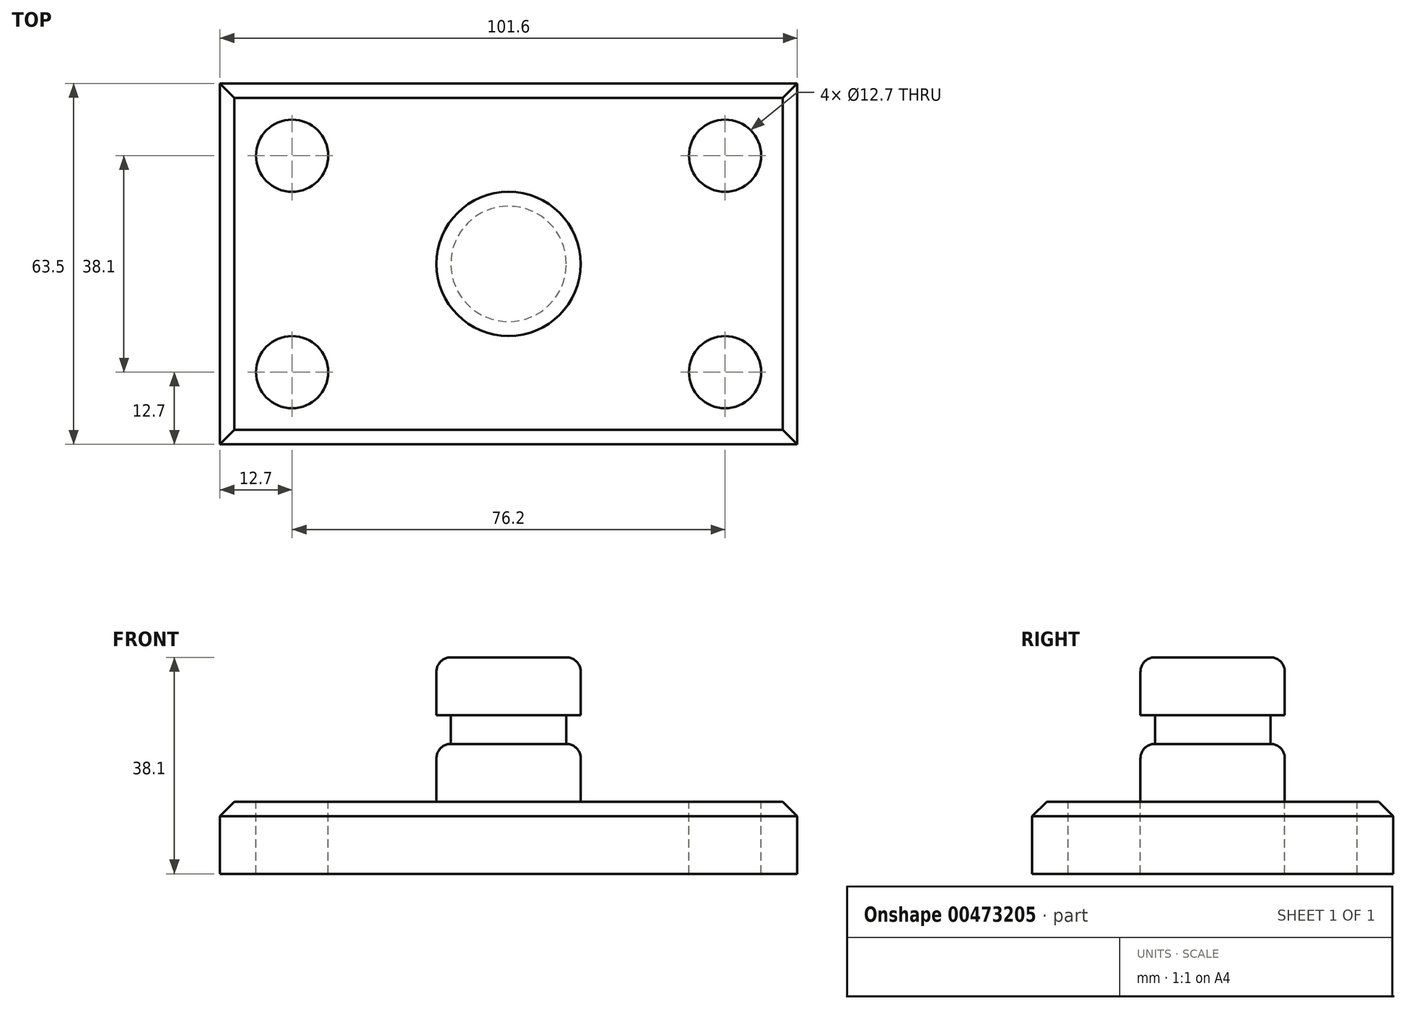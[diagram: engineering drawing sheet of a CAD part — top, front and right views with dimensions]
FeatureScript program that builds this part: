
annotation { "Feature Type Name" : "Feature", "Feature Type Description" : "" }
export const myFeature = defineFeature(function(context is Context, id is Id, definition is map)
    precondition{}
    {
        {
            var Q0;
            Q0=qCreatedBy(makeId("Top.planeOp"),FACE);
            var sketch = newSketch(context, id + "F0", { "sketchPlane" : qUnion([Q0])});
            skLineSegment(sketch, "E0.bottom", {"start": v(50.8, -31.75) * mm, "end": v(-50.8, -31.75) * mm});
            skLineSegment(sketch, "E0.top", {"start": v(50.8, 31.75) * mm, "end": v(-50.8, 31.75) * mm});
            skLineSegment(sketch, "E0.left", {"start": v(50.8, -31.75) * mm, "end": v(50.8, 31.75) * mm});
            skLineSegment(sketch, "E0.right", {"start": v(-50.8, -31.75) * mm, "end": v(-50.8, 31.75) * mm});
            skPoint(sketch, "E0.middle", {"position": v(0, 0) * mm});
            skSolve(sketch);
        }
        {
            var Q0;
            Q0=makeQuery(id+"F0.imprint","IMPRINT",FACE,{"disambiguationData":[TD([[makeQuery(id+"F0.imprint","IMPRINT",EDGE,{"derivedFrom":sQuery(id+"F0.wireOp",EDGE,"E0.bottom")}),-1.0]])]});
            extrude(context, id + "F1", {"entities" : qUnion([Q0]), "depth" : 12.7 * mm});
        }
        {
            var Q0;
            Q0=makeQuery(id+"F1.opExtrude","CAP_FACE",FACE,{"disambiguationData":[OSD([sQuery(id+"F0.wireOp",EDGE,"E0.bottom"),sQuery(id+"F0.wireOp",EDGE,"E0.top"),sQuery(id+"F0.wireOp",EDGE,"E0.left"),sQuery(id+"F0.wireOp",EDGE,"E0.right")])],"isStart":false});
            var sketch = newSketch(context, id + "F2", { "sketchPlane" : qUnion([Q0])});
            skCircle(sketch, "E1", {"center": v(-38.1, 19.05) * mm, "radius": 6.35 * mm});
            skCircle(sketch, "E2", {"center": v(38.1, 19.05) * mm, "radius": 6.35 * mm});
            skCircle(sketch, "E3", {"center": v(38.1, -19.05) * mm, "radius": 6.35 * mm});
            skCircle(sketch, "E4", {"center": v(-38.1, -19.05) * mm, "radius": 6.35 * mm});
            skSolve(sketch);
        }
        {
            var Q0;
            Q0 = qSketchRegion(id + "F2", true);
            extrude(context, id + "F3", {"entities" : qUnion([Q0]), "operationType" : NewBodyOperationType.REMOVE, "endBound" : BoundingType.THROUGH_ALL, "oppositeDirection" : true, "depth" : 25.4 * mm});
        }
        {
            var Q0;
            Q0=qCreatedBy(makeId("Front.planeOp"),FACE);
            var sketch = newSketch(context, id + "F4", { "sketchPlane" : qUnion([Q0])});
            skLineSegment(sketch, "E5.bottom", {"start": v(0, 12.7) * mm, "end": v(12.7, 12.7) * mm});
            skLineSegment(sketch, "E5.top", {"start": v(0, 38.1) * mm, "end": v(12.7, 38.1) * mm});
            skLineSegment(sketch, "E5.left", {"start": v(0, 12.7) * mm, "end": v(0, 38.1) * mm});
            skLineSegment(sketch, "E5.right", {"start": v(12.7, 12.7) * mm, "end": v(12.7, 38.1) * mm});
            skSolve(sketch);
        }
        {
            var Q0;
            Q0=makeQuery(id+"F4.imprint","IMPRINT",FACE,{"disambiguationData":[TD([[makeQuery(id+"F4.imprint","IMPRINT",EDGE,{"derivedFrom":sQuery(id+"F4.wireOp",EDGE,"E5.bottom")}),1.0]])]});
            var Q1;
            Q1=sQuery(id+"F4.wireOp",EDGE,"E5.left");
            revolve(context, id + "F5", {"operationType" : NewBodyOperationType.ADD, "entities" : qUnion([Q0]), "axis" : qUnion([Q1]), "revolveType" : RevolveType.FULL});
        }
        {
            var Q0;
            Q0=qCreatedBy(makeId("Front.planeOp"),FACE);
            var sketch = newSketch(context, id + "F6", { "sketchPlane" : qUnion([Q0])});
            skLineSegment(sketch, "E6.bottom", {"start": v(17.43, 27.94) * mm, "end": v(10.16, 27.94) * mm});
            skLineSegment(sketch, "E6.top", {"start": v(17.43, 22.86) * mm, "end": v(10.16, 22.86) * mm});
            skLineSegment(sketch, "E6.left", {"start": v(17.43, 27.94) * mm, "end": v(17.43, 22.86) * mm});
            skLineSegment(sketch, "E6.right", {"start": v(10.16, 27.94) * mm, "end": v(10.16, 22.86) * mm});
            skLineSegment(sketch, "E7", {"start": v(12.7, 38.1) * mm, "end": v(12.7, 12.7) * mm});
            skSolve(sketch);
        }
        {
            var Q0;
            Q0 = qSketchRegion(id + "F6", true);
            var Q1;
            Q1=makeQuery(id+"F5.opRevolve","SWEPT_FACE",FACE,{"disambiguationData":[OSD([sQuery(id+"F4.wireOp",EDGE,"E5.right")])]});
            revolve(context, id + "F7", {"operationType" : NewBodyOperationType.REMOVE, "entities" : qUnion([Q0]), "axis" : qUnion([Q1]), "revolveType" : RevolveType.FULL, "oppositeDirection" : true});
        }
        {
            var Q0;
            Q0=makeQuery(id+"F5.opRevolve","SWEPT_EDGE",EDGE,{"disambiguationData":[OSD([sQuery(id+"F4.wireOp",EDGE,"E5.bottom"),sQuery(id+"F4.wireOp",EDGE,"E5.right")])]});
            var Q1;
            Q1=makeQuery(id+"F7.boolean.opBoolean","INTERSECT",EDGE,{"derivedFrom":[makeQuery(id+"F5.opRevolve","SWEPT_FACE",FACE,{"disambiguationData":[OSD([sQuery(id+"F4.wireOp",EDGE,"E5.right")])]}),makeQuery(id+"F7.opRevolve","SWEPT_FACE",FACE,{"disambiguationData":[OSD([sQuery(id+"F6.wireOp",EDGE,"E6.top")])]})]});
            fillet(context, id + "F8", {"entities" : qUnion([Q0, Q1]), "radius" : 2.54 * mm, "tangentPropagation" : true, "allowEdgeOverflow" : false});
        }
        {
            var Q0;
            Q0=makeQuery(id+"F5.opRevolve","SWEPT_EDGE",EDGE,{"disambiguationData":[OSD([sQuery(id+"F4.wireOp",EDGE,"E5.top"),sQuery(id+"F4.wireOp",EDGE,"E5.right")])]});
            fillet(context, id + "F9", {"entities" : qUnion([Q0]), "radius" : 2.54 * mm, "tangentPropagation" : true, "allowEdgeOverflow" : false});
        }
        {
            var Q0;
            Q0=makeQuery(id+"F1.opExtrude","CAP_EDGE",EDGE,{"disambiguationData":[OSD([sQuery(id+"F0.wireOp",EDGE,"E0.right")])],"isStart":false});
            var Q1;
            Q1=makeQuery(id+"F1.opExtrude","CAP_EDGE",EDGE,{"disambiguationData":[OSD([sQuery(id+"F0.wireOp",EDGE,"E0.bottom")])],"isStart":false});
            var Q2;
            Q2=makeQuery(id+"F1.opExtrude","CAP_EDGE",EDGE,{"disambiguationData":[OSD([sQuery(id+"F0.wireOp",EDGE,"E0.top")])],"isStart":false});
            var Q3;
            Q3=makeQuery(id+"F1.opExtrude","CAP_EDGE",EDGE,{"disambiguationData":[OSD([sQuery(id+"F0.wireOp",EDGE,"E0.left")])],"isStart":false});
            chamfer(context, id + "F10", {"entities" : qUnion([Q0, Q1, Q2, Q3]), "width" : 2.54 * mm, "tangentPropagation" : true});
        }
    });
